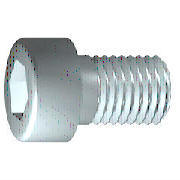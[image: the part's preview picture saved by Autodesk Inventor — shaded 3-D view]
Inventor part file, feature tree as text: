
AUTODESK INVENTOR PART (.ipt)
format: ipt  version: 2016 (Build 200138000, 138)  size: 198,144 bytes
history: native  units: mm (DEFAULTED — no unit token found)
features: sketch x2, extrude x1, plane x1, fillet x1
ambient origin geometry x7: Origin, YZ Plane, XY Plane, X Axis, Y Axis, Z Axis, Center Point
bodies: Solid1 (feature_tree), Body (feature_tree)
feature tree (5):
  extrude  "Slot"  Depth=6.0mm
  plane  "Work Plane1"
  fillet  "Fillet2"  Radius=6.0mm
  sketch  "Sketch1"  dims[d1=17.5mm d2=0.61355mm d3=6.0mm]
  sketch  "Sketch2"  dims[d4=3.0mm d5=60.0deg d6=6.0mm d7=6.0mm d8=5.773503mm d9=10.0mm d10=90.0deg d11=10.0mm d12=0.0mm d13=17.5mm d14=0.0mm d15=0.61345mm d16=0.61345mm d17=0.6mm d19=0.0mm d26=20.0mm d27=45.0deg d28=0.0mm d29=0.0mm d30=0.1mm]
